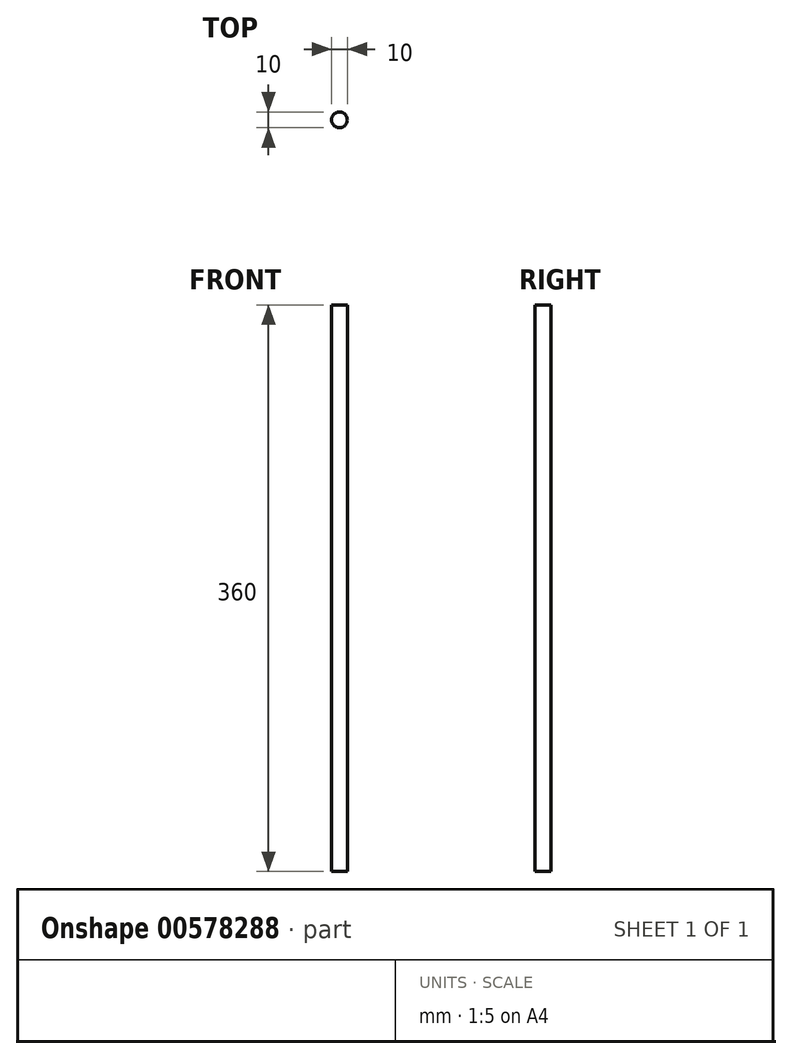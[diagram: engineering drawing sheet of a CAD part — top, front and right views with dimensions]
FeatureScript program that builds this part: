
annotation { "Feature Type Name" : "Feature", "Feature Type Description" : "" }
export const myFeature = defineFeature(function(context is Context, id is Id, definition is map)
    precondition{}
    {
        {
            var Q0;
            Q0=qCreatedBy(makeId("Top.planeOp"),FACE);
            var sketch = newSketch(context, id + "F0", { "sketchPlane" : qUnion([Q0])});
            skCircle(sketch, "E0", {"center": v(0, 0) * mm, "radius": 5 * mm});
            skSolve(sketch);
        }
        {
            var Q0;
            Q0=qSketchRegion(id+"F0",true);
            extrude(context, id + "F1", {"entities" : qUnion([Q0]), "depth" : 360 * mm, "offsetDistance" : 25 * mm});
        }
    });
